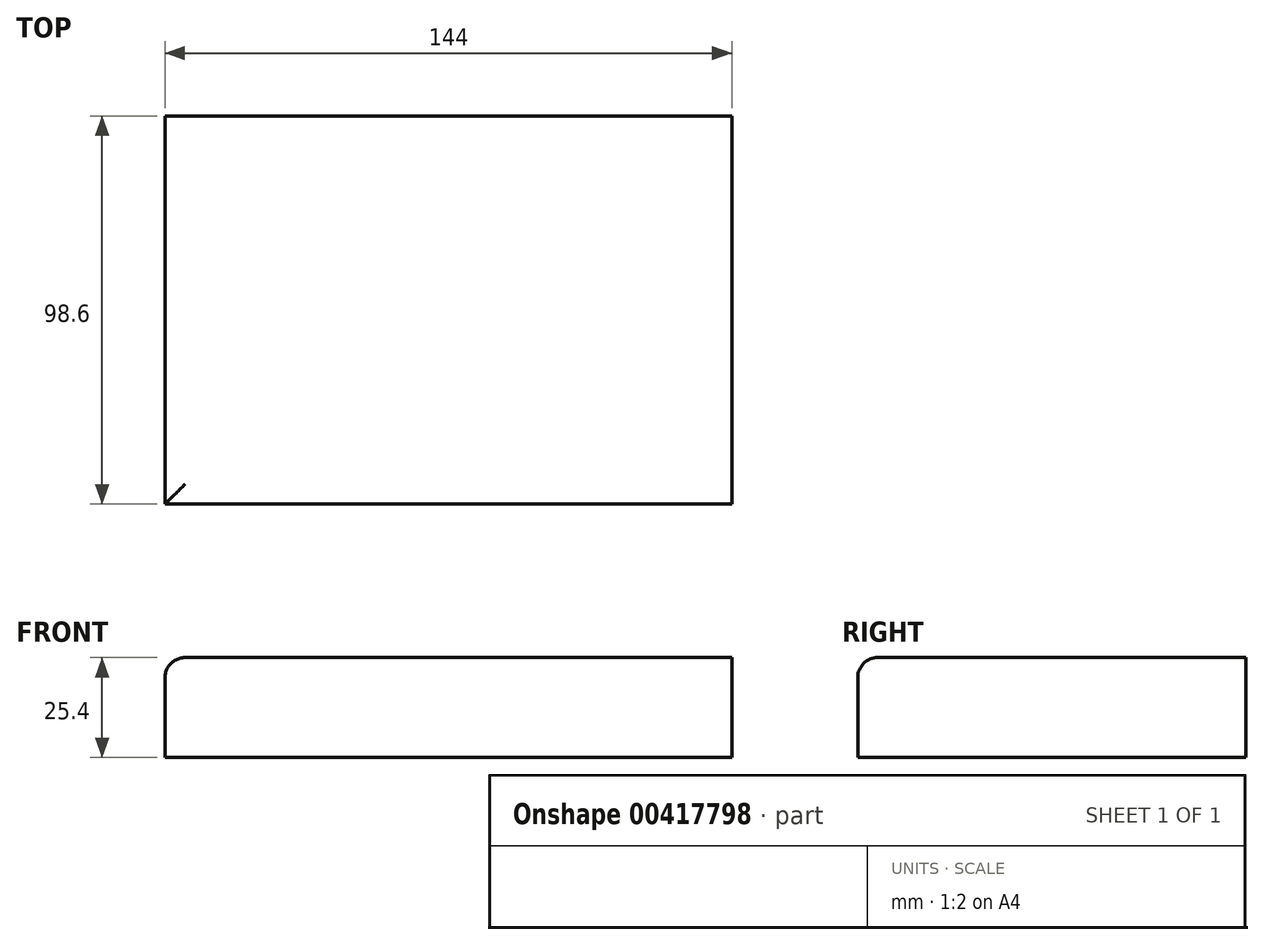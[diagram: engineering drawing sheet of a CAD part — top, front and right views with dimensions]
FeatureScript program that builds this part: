
annotation { "Feature Type Name" : "Feature", "Feature Type Description" : "" }
export const myFeature = defineFeature(function(context is Context, id is Id, definition is map)
    precondition{}
    {
        {
            var Q0;
            Q0=qCreatedBy(makeId("Top.planeOp"),FACE);
            var sketch = newSketch(context, id + "F0", { "sketchPlane" : qUnion([Q0])});
            skLineSegment(sketch, "E0.bottom", {"start": v(-71.9, 50.64) * mm, "end": v(72.1, 50.64) * mm});
            skLineSegment(sketch, "E0.top", {"start": v(-71.9, -47.96) * mm, "end": v(72.1, -47.96) * mm});
            skLineSegment(sketch, "E0.left", {"start": v(-71.9, 50.64) * mm, "end": v(-71.9, -47.96) * mm});
            skLineSegment(sketch, "E0.right", {"start": v(72.1, 50.64) * mm, "end": v(72.1, -47.96) * mm});
            skSolve(sketch);
        }
        {
            var Q0;
            Q0 = qSketchRegion(id + "F0", true);
            extrude(context, id + "F1", {"entities" : qUnion([Q0]), "depth" : 25.4 * mm});
        }
        {
            var Q0;
            Q0=makeQuery(id+"F1.opExtrude","CAP_EDGE",EDGE,{"disambiguationData":[OSD([sQuery(id+"F0.wireOp",EDGE,"E0.left")])],"isStart":false});
            var Q1;
            Q1=makeQuery(id+"F1.opExtrude","CAP_EDGE",EDGE,{"disambiguationData":[OSD([sQuery(id+"F0.wireOp",EDGE,"E0.top")])],"isStart":false});
            fillet(context, id + "F2", {"entities" : qUnion([Q0, Q1]), "radius" : 5.08 * mm, "tangentPropagation" : true, "allowEdgeOverflow" : false});
        }
    });
